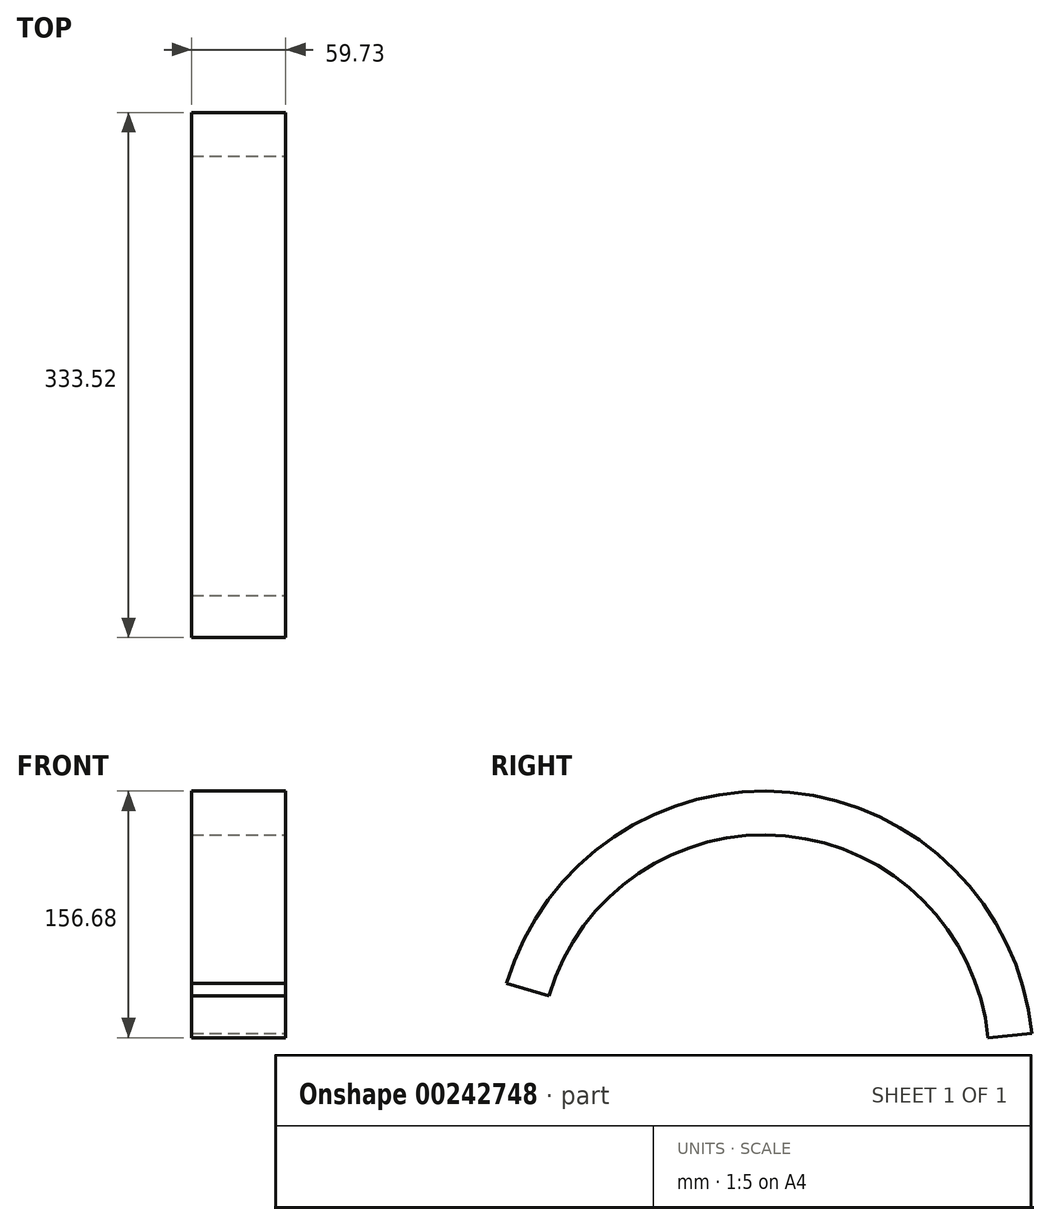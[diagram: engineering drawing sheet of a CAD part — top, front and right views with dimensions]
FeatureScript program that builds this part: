
annotation { "Feature Type Name" : "Feature", "Feature Type Description" : "" }
export const myFeature = defineFeature(function(context is Context, id is Id, definition is map)
    precondition{}
    {
        {
            var Q0;
            Q0=qCreatedBy(makeId("Front.planeOp"),FACE);
            var sketch = newSketch(context, id + "F0", { "sketchPlane" : qUnion([Q0])});
            skLineSegment(sketch, "E0.bottom", {"start": v(-29.33, 13.41) * mm, "end": v(30.4, 13.41) * mm});
            skLineSegment(sketch, "E0.top", {"start": v(-29.33, -14.49) * mm, "end": v(30.4, -14.49) * mm});
            skLineSegment(sketch, "E0.left", {"start": v(-29.33, 13.41) * mm, "end": v(-29.33, -14.49) * mm});
            skLineSegment(sketch, "E0.right", {"start": v(30.4, 13.41) * mm, "end": v(30.4, -14.49) * mm});
            skSolve(sketch);
        }
        {
            var Q0;
            Q0=qCreatedBy(makeId("Right.planeOp"),FACE);
            var sketch = newSketch(context, id + "F1", { "sketchPlane" : qUnion([Q0])});
            skArc(sketch, "E1", {"start": v(0, 0) * mm, "mid": v(-94.12, -31.28) * mm, "end": v(-150.8, -112.66) * mm});
            skArc(sketch, "E2", {"start": v(-150.8, -112.66) * mm, "mid": v(14.87, -0.7) * mm, "end": v(156.5, -141.85) * mm});
            skSolve(sketch);
        }
        {
            var Q0;
            Q0=makeQuery(id+"F0.imprint","IMPRINT",FACE,{"disambiguationData":[TD([[makeQuery(id+"F0.imprint","IMPRINT",EDGE,{"derivedFrom":sQuery(id+"F0.wireOp",EDGE,"E0.bottom")}),-1.0]])]});
            var Q1;
            Q1=sQuery(id+"F1.wireOp",EDGE,"E2");
            sweep(context, id + "F2", {"profiles" : qUnion([Q0]), "path" : qUnion([Q1])});
        }
    });
